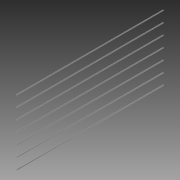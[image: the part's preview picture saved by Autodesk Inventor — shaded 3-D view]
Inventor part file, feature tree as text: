
AUTODESK INVENTOR PART (.ipt)
format: ipt  version: 2015 (Build 190159000, 159)  size: 84,992 bytes
history: native  units: in
note: dims shown in document units (in); Inventor stores cm internally (conversion verified against a paired STEP export)
features: extrude x1, sketch x1
ambient origin geometry x8: Origin, YZ Plane, XZ Plane, XY Plane, X Axis, Y Axis, Z Axis, Center Point
bodies: Body1 (feature_tree)
feature tree (2):
  extrude  "Extrusion2"  Depth=4.0in
  sketch  "Sketch1"  dims[d0=0.375in d3=4.0in d4=4.0in d5=4.0in d6=4.0in d7=4.0in d8=54.22in d9=0.0in d10=4.0in]
